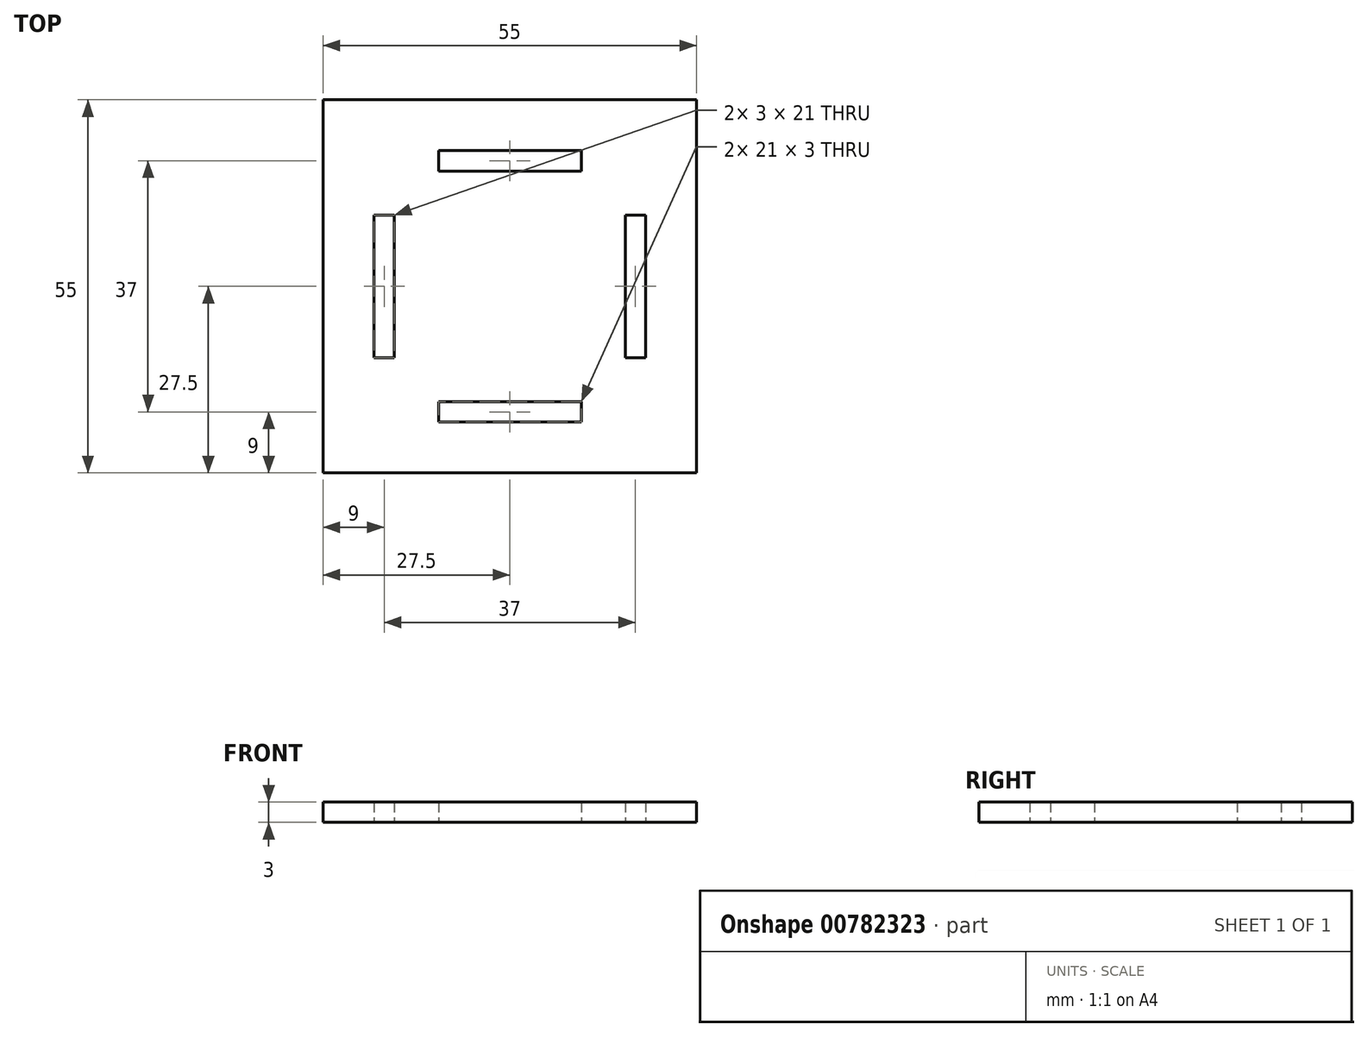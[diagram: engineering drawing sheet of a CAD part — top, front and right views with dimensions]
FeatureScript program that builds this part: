
annotation { "Feature Type Name" : "Feature", "Feature Type Description" : "" }
export const myFeature = defineFeature(function(context is Context, id is Id, definition is map)
    precondition{}
    {
        {
            var Q0;
            Q0=qCreatedBy(makeId("Top.planeOp"),FACE);
            var sketch = newSketch(context, id + "F0", { "sketchPlane" : qUnion([Q0])});
            skLineSegment(sketch, "E0.bottom", {"start": v(27.5, 27.5) * mm, "end": v(-27.5, 27.5) * mm});
            skLineSegment(sketch, "E0.top", {"start": v(27.5, -27.5) * mm, "end": v(-27.5, -27.5) * mm});
            skLineSegment(sketch, "E0.left", {"start": v(27.5, 27.5) * mm, "end": v(27.5, -27.5) * mm});
            skLineSegment(sketch, "E0.right", {"start": v(-27.5, 27.5) * mm, "end": v(-27.5, -27.5) * mm});
            skPoint(sketch, "E0.middle", {"position": v(0, 0) * mm});
            skLineSegment(sketch, "E1.bottom", {"start": v(-20, 10.5) * mm, "end": v(-17, 10.5) * mm});
            skLineSegment(sketch, "E1.top", {"start": v(-20, -10.5) * mm, "end": v(-17, -10.5) * mm});
            skLineSegment(sketch, "E1.left", {"start": v(-20, 10.5) * mm, "end": v(-20, -10.5) * mm});
            skLineSegment(sketch, "E1.right", {"start": v(-17, 10.5) * mm, "end": v(-17, -10.5) * mm});
            skLineSegment(sketch, "E2.bottom", {"start": v(-10.5, 20) * mm, "end": v(10.5, 20) * mm});
            skLineSegment(sketch, "E2.top", {"start": v(-10.5, 17) * mm, "end": v(10.5, 17) * mm});
            skLineSegment(sketch, "E2.left", {"start": v(-10.5, 20) * mm, "end": v(-10.5, 17) * mm});
            skLineSegment(sketch, "E2.right", {"start": v(10.5, 20) * mm, "end": v(10.5, 17) * mm});
            skLineSegment(sketch, "E3.MirrorCS", {"start": v(-10.5, -20) * mm, "end": v(-10.5, -17) * mm});
            skLineSegment(sketch, "E4.MirrorCS", {"start": v(-10.5, -20) * mm, "end": v(10.5, -20) * mm});
            skLineSegment(sketch, "E5.MirrorCS", {"start": v(10.5, -20) * mm, "end": v(10.5, -17) * mm});
            skLineSegment(sketch, "E6.MirrorCS", {"start": v(-10.5, -17) * mm, "end": v(10.5, -17) * mm});
            skLineSegment(sketch, "E7.MirrorCS", {"start": v(20, 10.5) * mm, "end": v(17, 10.5) * mm});
            skLineSegment(sketch, "E8.MirrorCS", {"start": v(17, 10.5) * mm, "end": v(17, -10.5) * mm});
            skLineSegment(sketch, "E9.MirrorCS", {"start": v(20, -10.5) * mm, "end": v(17, -10.5) * mm});
            skLineSegment(sketch, "E10.MirrorCS", {"start": v(20, 10.5) * mm, "end": v(20, -10.5) * mm});
            skSolve(sketch);
        }
        {
            var Q0;
            Q0=makeQuery(id+"F0.imprint","IMPRINT",FACE,{"disambiguationData":[TD([[makeQuery(id+"F0.imprint","IMPRINT",EDGE,{"derivedFrom":sQuery(id+"F0.wireOp",EDGE,"E0.bottom")}),1.0]])]});
            extrude(context, id + "F1", {"entities" : qUnion([Q0]), "depth" : 3 * mm, "offsetDistance" : 25 * mm});
        }
    });
